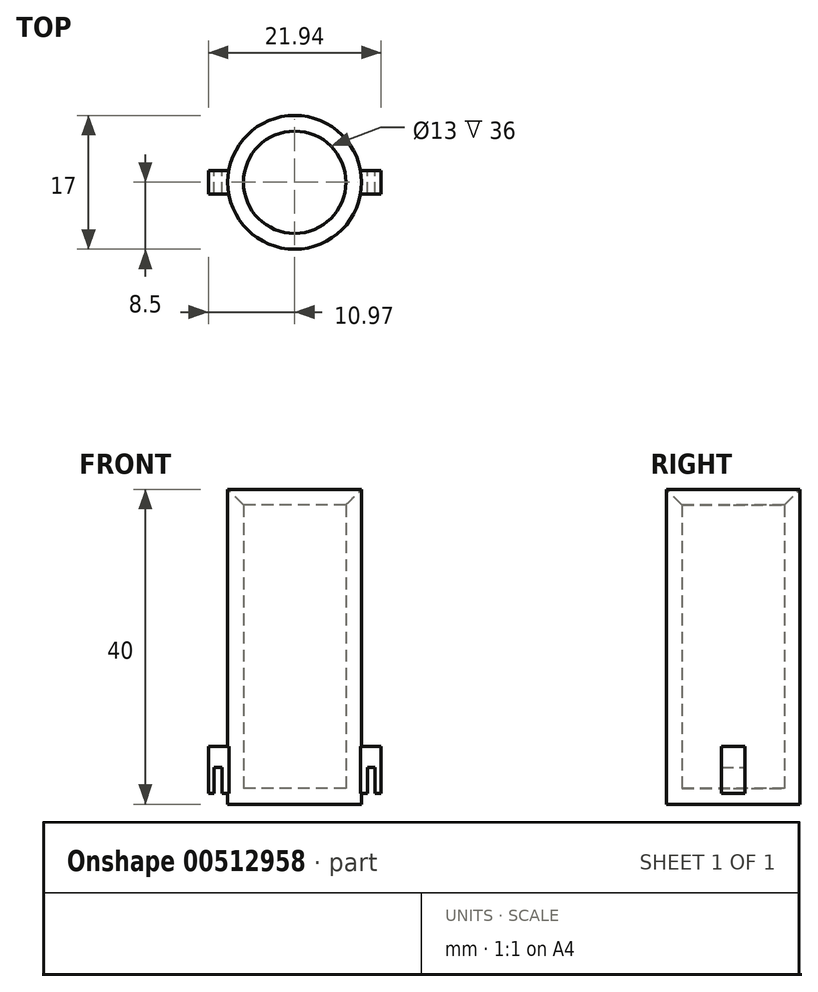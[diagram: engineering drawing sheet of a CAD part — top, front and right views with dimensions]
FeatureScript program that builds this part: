
annotation { "Feature Type Name" : "Feature", "Feature Type Description" : "" }
export const myFeature = defineFeature(function(context is Context, id is Id, definition is map)
    precondition{}
    {
        {
            var Q0;
            Q0=qCreatedBy(makeId("Top.planeOp"),FACE);
            var sketch = newSketch(context, id + "F0", { "sketchPlane" : qUnion([Q0])});
            skCircle(sketch, "E0", {"center": v(0, 0) * mm, "radius": 8.5 * mm});
            skSolve(sketch);
        }
        {
            var Q0;
            Q0=makeQuery(id+"F0.imprint","IMPRINT",FACE,{"disambiguationData":[TD([[makeQuery(id+"F0.imprint","IMPRINT",EDGE,{"derivedFrom":sQuery(id+"F0.wireOp",EDGE,"E0")}),1.0]])]});
            extrude(context, id + "F1", {"entities" : qUnion([Q0]), "depth" : 40 * mm, "offsetDistance" : 25 * mm});
        }
        {
            var Q0;
            Q0=makeQuery(id+"F1.opExtrude","CAP_FACE",FACE,{"disambiguationData":[OSD([sQuery(id+"F0.wireOp",EDGE,"E0")])],"isStart":false});
            shell(context, id + "F2", {"entities" : qUnion([Q0]), "thickness" : 2 * mm});
        }
        {
            var Q0;
            {var subQ0=sQuery(id+"F0.wireOp",EDGE,"E0");Q0=makeQuery(id+"F2.opShell","OFFSET_EDGE",EDGE,{"disambiguationData":[OSD([subQ0]),TDD([makeQuery(id+"F1.opExtrude","CAP_EDGE",EDGE,{"disambiguationData":[OSD([subQ0])],"isStart":false})])]});}
            chamfer(context, id + "F3", {"entities" : qUnion([Q0]), "width" : 2 * mm, "tangentPropagation" : true});
        }
        {
            var Q0;
            Q0=qCreatedBy(makeId("Front.planeOp"),FACE);
            var sketch = newSketch(context, id + "F4", { "sketchPlane" : qUnion([Q0])});
            skLineSegment(sketch, "E1", {"start": v(0, 45.05) * mm, "end": v(0, -10.1) * mm, "construction": true});
            skLineSegment(sketch, "E2.bottom", {"start": v(-8.27, 7.36) * mm, "end": v(-10.97, 7.36) * mm});
            skLineSegment(sketch, "E2.top", {"start": v(-8.27, 1.36) * mm, "end": v(-9.22, 1.36) * mm});
            skLineSegment(sketch, "E2.left", {"start": v(-8.27, 7.36) * mm, "end": v(-8.27, 1.36) * mm});
            skLineSegment(sketch, "E2.right", {"start": v(-10.97, 7.36) * mm, "end": v(-10.97, 1.36) * mm});
            skLineSegment(sketch, "E3.bottom", {"start": v(-9.22, 4.64) * mm, "end": v(-10.23, 4.64) * mm});
            skLineSegment(sketch, "E3.left", {"start": v(-9.22, 4.64) * mm, "end": v(-9.22, 1.36) * mm});
            skLineSegment(sketch, "E3.right", {"start": v(-10.23, 4.64) * mm, "end": v(-10.23, 1.36) * mm});
            skLineSegment(sketch, "E4.trimOffspring", {"start": v(-10.23, 1.36) * mm, "end": v(-10.97, 1.36) * mm});
            skLineSegment(sketch, "E5.MirrorCS", {"start": v(8.27, 7.36) * mm, "end": v(10.97, 7.36) * mm});
            skLineSegment(sketch, "E6.MirrorCS", {"start": v(8.27, 7.36) * mm, "end": v(8.27, 1.36) * mm});
            skLineSegment(sketch, "E7.MirrorCS", {"start": v(9.22, 4.64) * mm, "end": v(10.23, 4.64) * mm});
            skLineSegment(sketch, "E8.MirrorCS", {"start": v(9.22, 4.64) * mm, "end": v(9.22, 1.36) * mm});
            skLineSegment(sketch, "E9.MirrorCS", {"start": v(8.27, 1.36) * mm, "end": v(9.22, 1.36) * mm});
            skLineSegment(sketch, "E10.MirrorCS", {"start": v(10.23, 1.36) * mm, "end": v(10.97, 1.36) * mm});
            skLineSegment(sketch, "E11.MirrorCS", {"start": v(10.97, 7.36) * mm, "end": v(10.97, 1.36) * mm});
            skLineSegment(sketch, "E12.MirrorCS", {"start": v(10.23, 4.64) * mm, "end": v(10.23, 1.36) * mm});
            skSolve(sketch);
        }
        {
            var Q0;
            Q0=makeQuery(id+"F4.imprint","IMPRINT",FACE,{"disambiguationData":[TD([[makeQuery(id+"F4.imprint","IMPRINT",EDGE,{"derivedFrom":sQuery(id+"F4.wireOp",EDGE,"E2.bottom")}),1.0]])]});
            var Q1;
            Q1=makeQuery(id+"F4.imprint","IMPRINT",FACE,{"disambiguationData":[TD([[makeQuery(id+"F4.imprint","IMPRINT",EDGE,{"derivedFrom":sQuery(id+"F4.wireOp",EDGE,"E5.MirrorCS")}),-1.0]])]});
            extrude(context, id + "F5", {"entities" : qUnion([Q0, Q1]), "operationType" : NewBodyOperationType.ADD, "endBound" : BoundingType.SYMMETRIC, "depth" : 3 * mm, "offsetDistance" : 25 * mm});
        }
    });
